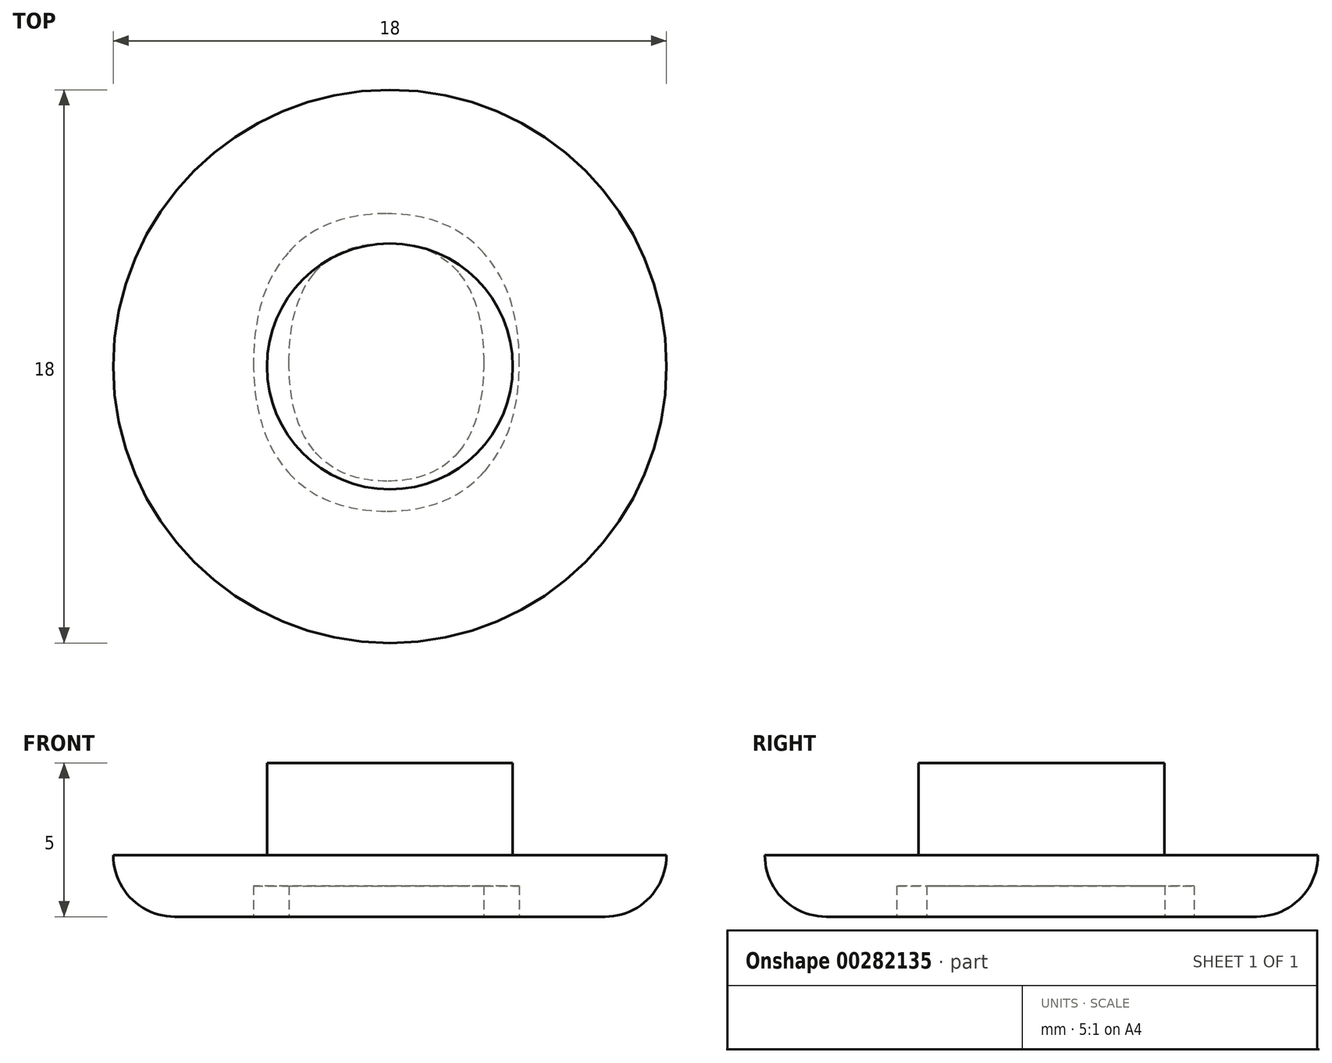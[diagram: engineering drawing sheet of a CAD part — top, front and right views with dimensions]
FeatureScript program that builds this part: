
annotation { "Feature Type Name" : "Feature", "Feature Type Description" : "" }
export const myFeature = defineFeature(function(context is Context, id is Id, definition is map)
    precondition{}
    {
        {
            var Q0;
            Q0=qCreatedBy(makeId("Top.planeOp"),FACE);
            var sketch = newSketch(context, id + "F0", { "sketchPlane" : qUnion([Q0])});
            skCircle(sketch, "E0", {"center": v(0, 0) * mm, "radius": 9 * mm});
            skSolve(sketch);
        }
        {
            var Q0;
            Q0=qSketchRegion(id+"F0",true);
            extrude(context, id + "F1", {"entities" : qUnion([Q0]), "depth" : 2 * mm});
        }
        {
            var Q0;
            Q0=makeQuery(id+"F1.opExtrude","CAP_FACE",FACE,{"disambiguationData":[OSD([sQuery(id+"F0.wireOp",EDGE,"E0")])],"isStart":false});
            var sketch = newSketch(context, id + "F2", { "sketchPlane" : qUnion([Q0])});
            skCircle(sketch, "E1", {"center": v(0, 0) * mm, "radius": 4 * mm});
            skSolve(sketch);
        }
        {
            var Q0;
            Q0=qSketchRegion(id+"F2",true);
            extrude(context, id + "F3", {"entities" : qUnion([Q0]), "operationType" : NewBodyOperationType.ADD, "depth" : 3 * mm});
        }
        {
            var Q0;
            Q0=makeQuery(id+"F1.opExtrude","CAP_EDGE",EDGE,{"disambiguationData":[OSD([sQuery(id+"F0.wireOp",EDGE,"E0")])],"isStart":true});
            fillet(context, id + "F4", {"entities" : qUnion([Q0]), "radius" : 2 * mm, "tangentPropagation" : true, "allowEdgeOverflow" : false});
        }
        {
            var Q0;
            Q0=makeQuery(id+"F1.opExtrude","CAP_FACE",FACE,{"disambiguationData":[OSD([sQuery(id+"F0.wireOp",EDGE,"E0")])],"isStart":true});
            var sketch = newSketch(context, id + "F5", { "sketchPlane" : qUnion([Q0])});
            skText(sketch, "E2", { "text": "O\n", "fontName": "OpenSans-Regular.ttf"});
            const initialGuessF5  = {"E2": [-0.00524, -0.00484, 1, 0, 0.00948]};
            skSetInitialGuess(sketch, initialGuessF5);
            skSolve(sketch);
        }
        {
            var Q0;
            Q0 = qSketchRegion(id + "F5", true);
            extrude(context, id + "F6", {"entities" : qUnion([Q0]), "operationType" : NewBodyOperationType.REMOVE, "oppositeDirection" : true, "depth" : 1 * mm});
        }
    });
